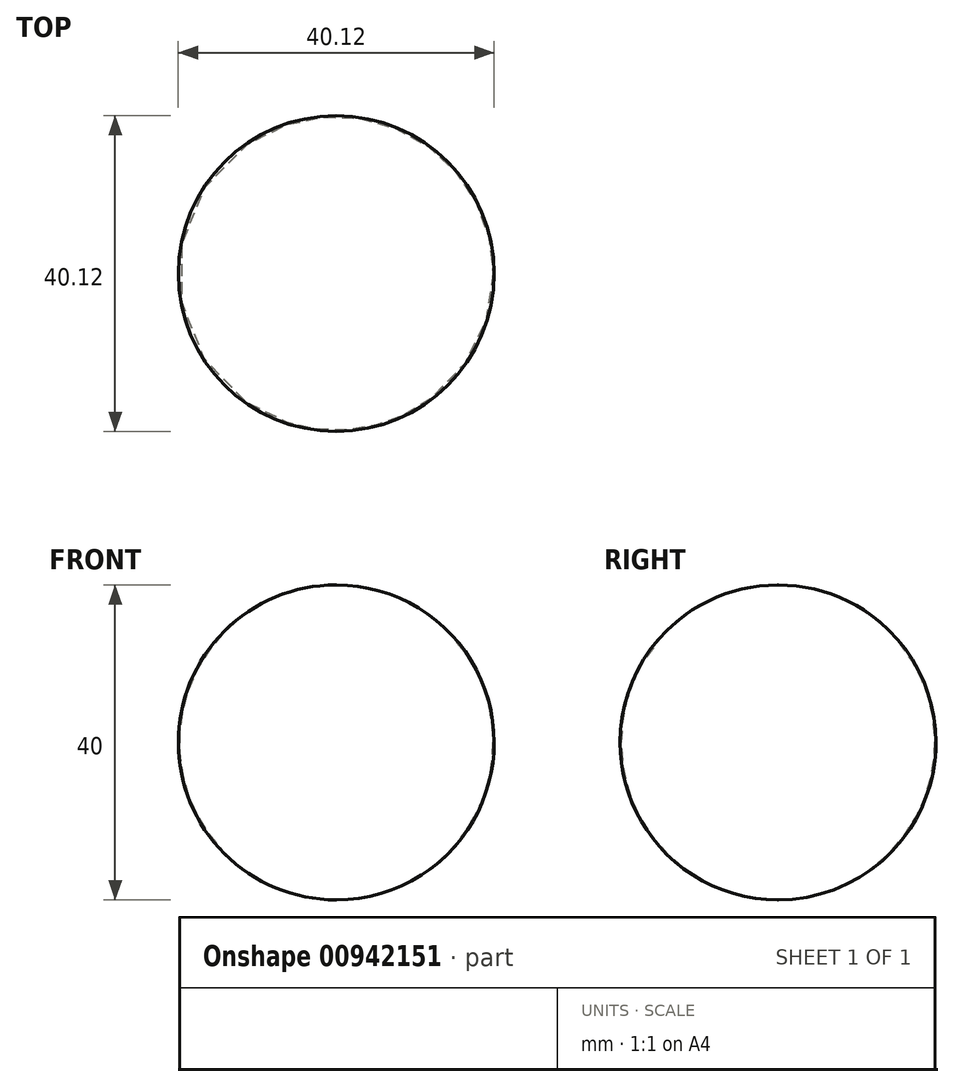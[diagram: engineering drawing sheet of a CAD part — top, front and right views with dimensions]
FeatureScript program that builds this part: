
annotation { "Feature Type Name" : "Feature", "Feature Type Description" : "" }
export const myFeature = defineFeature(function(context is Context, id is Id, definition is map)
    precondition{}
    {
        {
            var Q0;
            Q0=qCreatedBy(makeId("Front.planeOp"),FACE);
            var sketch = newSketch(context, id + "F0", { "sketchPlane" : qUnion([Q0])});
            skLineSegment(sketch, "E0", {"start": v(0, 0) * mm, "end": v(0, 40) * mm});
            skArc(sketch, "E1", {"start": v(0, 0) * mm, "mid": v(19.94, 20) * mm, "end": v(0, 40) * mm});
            skSolve(sketch);
        }
        {
            var Q0;
            Q0 = qSketchRegion(id + "F0", true);
            var Q1;
            Q1=sQuery(id+"F0.wireOp",EDGE,"E0");
            revolve(context, id + "F1", {"surfaceOperationType" : NewSurfaceOperationType.NEW, "entities" : qUnion([Q0]), "axis" : qUnion([Q1]), "revolveType" : RevolveType.FULL});
        }
    });
